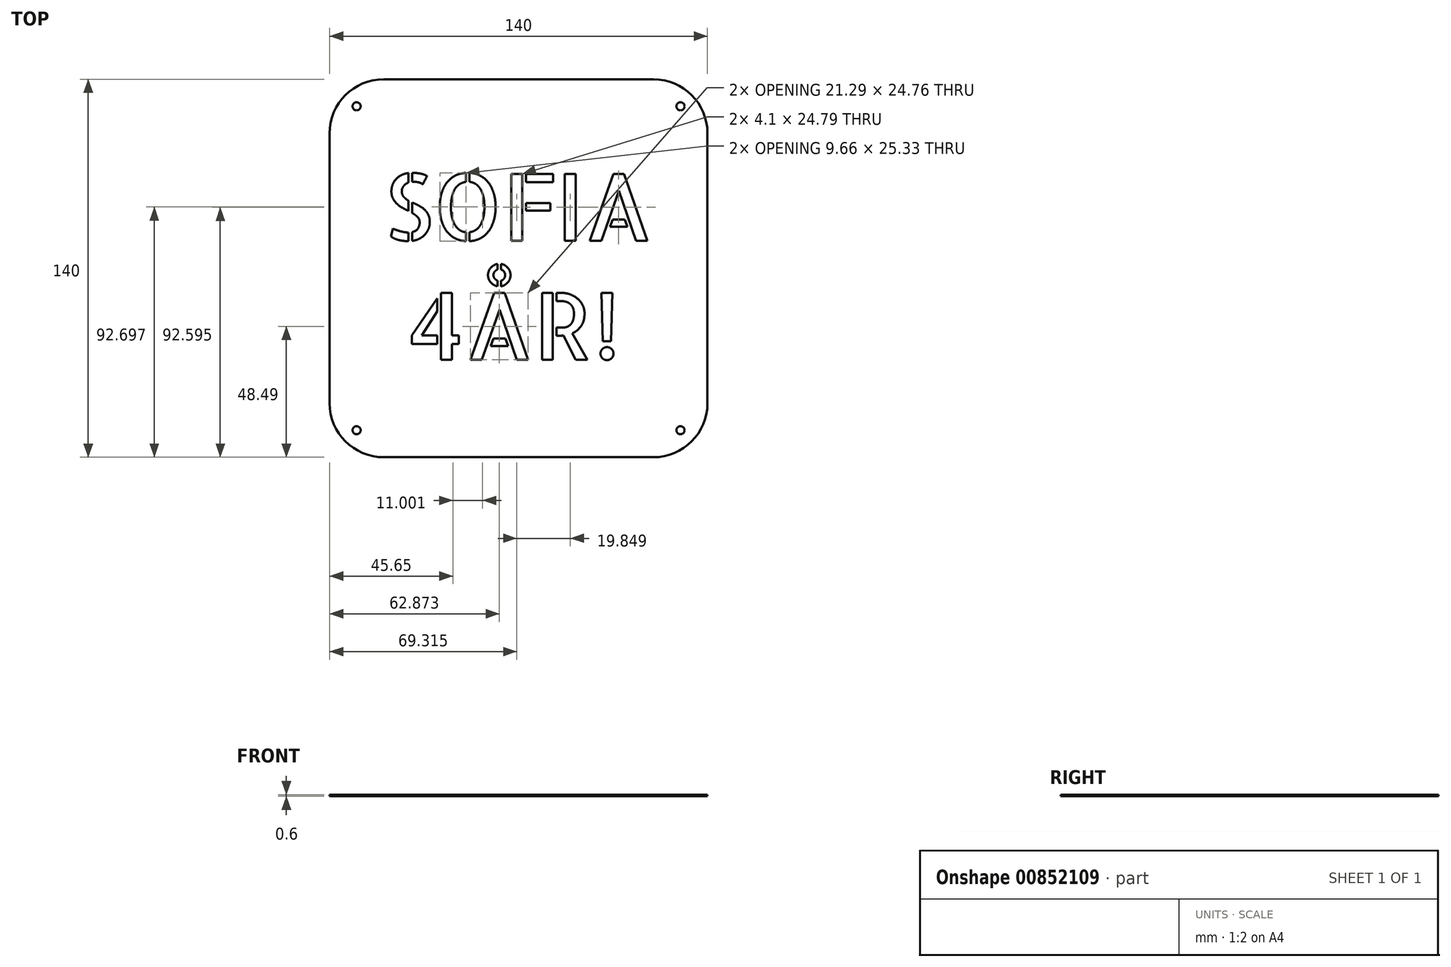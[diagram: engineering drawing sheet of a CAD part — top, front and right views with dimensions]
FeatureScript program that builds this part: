
annotation { "Feature Type Name" : "Feature", "Feature Type Description" : "" }
export const myFeature = defineFeature(function(context is Context, id is Id, definition is map)
    precondition{}
    {
        {
            var Q0;
            Q0=qCreatedBy(makeId("Top.planeOp"),FACE);
            var sketch = newSketch(context, id + "F0", { "sketchPlane" : qUnion([Q0])});
            skLineSegment(sketch, "E0.bottom", {"start": v(50, -70) * mm, "end": v(-50, -70) * mm});
            skLineSegment(sketch, "E0.top", {"start": v(50, 70) * mm, "end": v(-50, 70) * mm});
            skLineSegment(sketch, "E0.left", {"start": v(70, -50) * mm, "end": v(70, 50) * mm});
            skLineSegment(sketch, "E0.right", {"start": v(-70, -50) * mm, "end": v(-70, 50) * mm});
            skPoint(sketch, "E0.middle", {"position": v(0, 0) * mm});
            skText(sketch, "E1", { "text": "SOFIA\n 4ÅR!", "fontName": "AllertaStencil-Regular.ttf"});
            skPoint(sketch, "E2", {"position": v(0, 70) * mm});
            skCircle(sketch, "E3", {"center": v(-60, 60) * mm, "radius": 1.5 * mm});
            skCircle(sketch, "E4", {"center": v(60, 60) * mm, "radius": 1.5 * mm});
            skCircle(sketch, "E5", {"center": v(60, -60) * mm, "radius": 1.5 * mm});
            skCircle(sketch, "E6", {"center": v(-60, -60) * mm, "radius": 1.5 * mm});
            skPoint(sketch, "E7.visualSharp", {"position": v(-70, 70) * mm});
            skArc(sketch, "E7.filletArc", {"start": v(-50, 70) * mm, "mid": v(-64.14, 64.14) * mm, "end": v(-70, 50) * mm});
            skPoint(sketch, "E8.visualSharp", {"position": v(70, 70) * mm});
            skArc(sketch, "E8.filletArc", {"start": v(70, 50) * mm, "mid": v(64.14, 64.14) * mm, "end": v(50, 70) * mm});
            skPoint(sketch, "E9.visualSharp", {"position": v(70, -70) * mm});
            skArc(sketch, "E9.filletArc", {"start": v(50, -70) * mm, "mid": v(64.14, -64.14) * mm, "end": v(70, -50) * mm});
            skPoint(sketch, "E10.visualSharp", {"position": v(-70, -70) * mm});
            skArc(sketch, "E10.filletArc", {"start": v(-70, -50) * mm, "mid": v(-64.14, -64.14) * mm, "end": v(-50, -70) * mm});
            const initialGuessF0  = {"E1": [-0.05, 0.0102, 1, 0, 0.0248]};
            skSetInitialGuess(sketch, initialGuessF0);
            skSolve(sketch);
        }
        {
            var Q0;
            Q0 = qSketchRegion(id + "F0", true);
            extrude(context, id + "F1", {"entities" : qUnion([Q0]), "depth" : 0.6 * mm, "offsetDistance" : 25 * mm});
        }
    });
